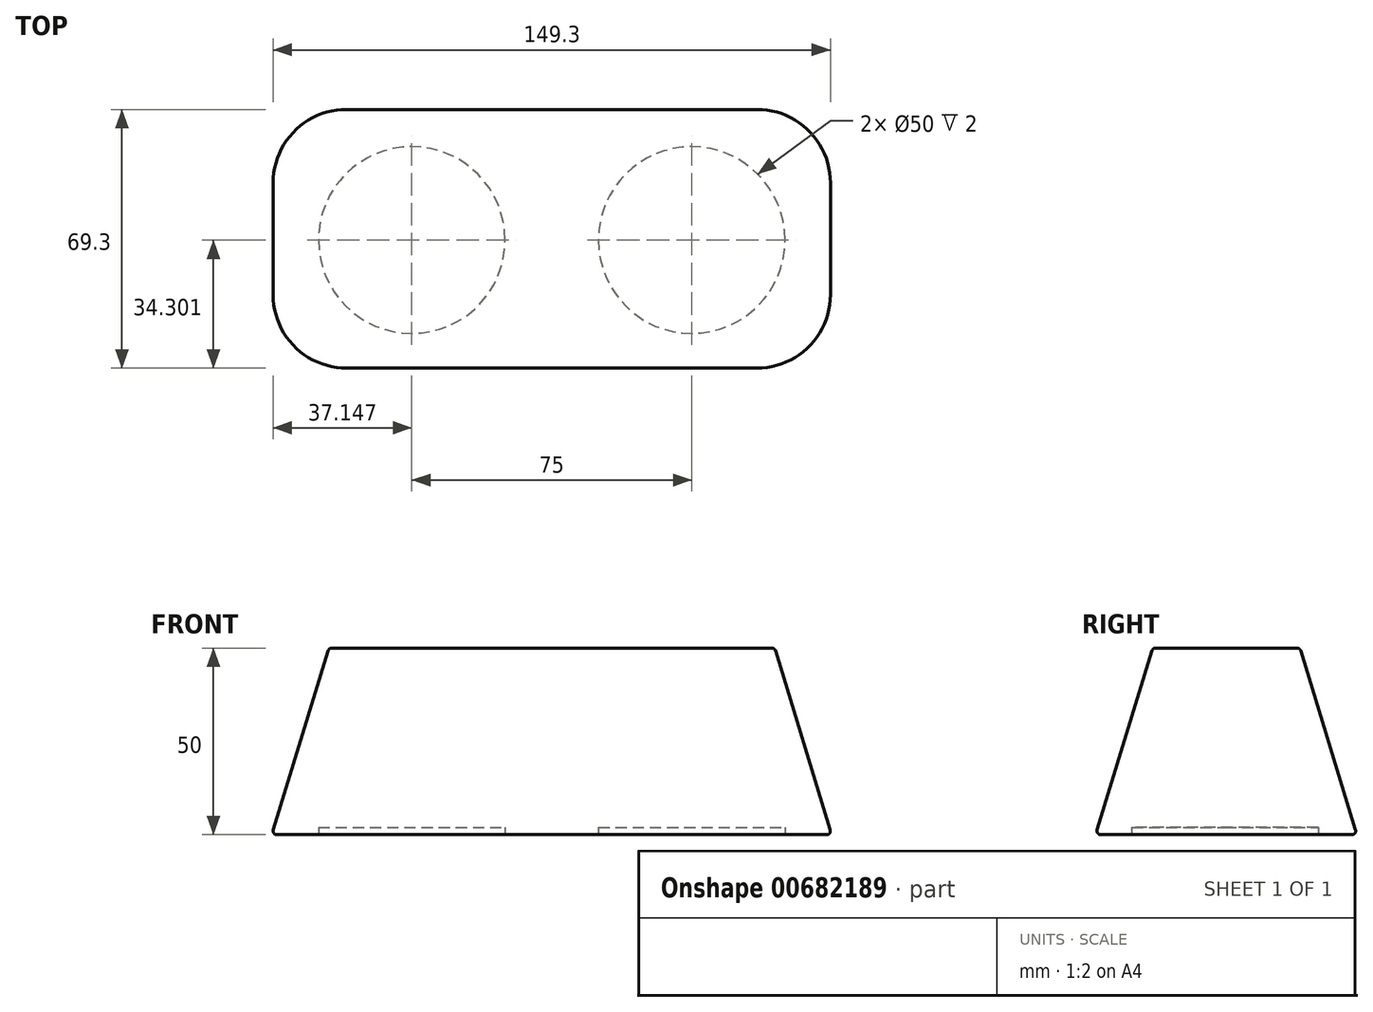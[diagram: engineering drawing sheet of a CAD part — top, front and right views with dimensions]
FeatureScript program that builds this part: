
annotation { "Feature Type Name" : "Feature", "Feature Type Description" : "" }
export const myFeature = defineFeature(function(context is Context, id is Id, definition is map)
    precondition{}
    {
        {
            var Q0;
            Q0=qCreatedBy(makeId("Top.planeOp"),FACE);
            var sketch = newSketch(context, id + "F0", { "sketchPlane" : qUnion([Q0])});
            skLineSegment(sketch, "E0.bottom", {"start": v(-57.37, 55.36) * mm, "end": v(52.63, 55.36) * mm});
            skLineSegment(sketch, "E0.top", {"start": v(-57.37, -14.64) * mm, "end": v(52.63, -14.64) * mm});
            skLineSegment(sketch, "E0.left", {"start": v(-77.37, 35.36) * mm, "end": v(-77.37, 5.36) * mm});
            skLineSegment(sketch, "E0.right", {"start": v(72.63, 35.36) * mm, "end": v(72.63, 5.36) * mm});
            skPoint(sketch, "E1.visualSharp", {"position": v(-77.37, 55.36) * mm});
            skArc(sketch, "E1.filletArc", {"start": v(-57.37, 55.36) * mm, "mid": v(-71.51, 49.5) * mm, "end": v(-77.37, 35.36) * mm});
            skPoint(sketch, "E2.visualSharp", {"position": v(72.63, -14.64) * mm});
            skArc(sketch, "E2.filletArc", {"start": v(52.63, -14.64) * mm, "mid": v(66.77, -8.78) * mm, "end": v(72.63, 5.36) * mm});
            skPoint(sketch, "E3.visualSharp", {"position": v(-77.37, -14.64) * mm});
            skArc(sketch, "E3.filletArc", {"start": v(-77.37, 5.36) * mm, "mid": v(-71.51, -8.78) * mm, "end": v(-57.37, -14.64) * mm});
            skPoint(sketch, "E4.visualSharp", {"position": v(72.63, 55.36) * mm});
            skArc(sketch, "E4.filletArc", {"start": v(72.63, 35.36) * mm, "mid": v(66.77, 49.5) * mm, "end": v(52.63, 55.36) * mm});
            skSolve(sketch);
        }
        {
            var Q0;
            Q0=makeQuery(id+"F0.imprint","IMPRINT",FACE,{"disambiguationData":[TD([[makeQuery(id+"F0.imprint","IMPRINT",EDGE,{"derivedFrom":sQuery(id+"F0.wireOp",EDGE,"E0.bottom")}),-1.0]])]});
            extrude(context, id + "F1", {"entities" : qUnion([Q0]), "depth" : 50 * mm, "offsetDistance" : 25 * mm, "hasDraft" : true, "draftAngle" : 17 * degree, "draftPullDirection" : true});
        }
        {
            var Q0;
            Q0=makeQuery(id+"F1.opExtrude","CAP_FACE",FACE,{"disambiguationData":[OSD([sQuery(id+"F0.wireOp",EDGE,"E0.bottom"),sQuery(id+"F0.wireOp",EDGE,"E0.top"),sQuery(id+"F0.wireOp",EDGE,"E0.left"),sQuery(id+"F0.wireOp",EDGE,"E0.right"),sQuery(id+"F0.wireOp",EDGE,"E1.filletArc"),sQuery(id+"F0.wireOp",EDGE,"E2.filletArc"),sQuery(id+"F0.wireOp",EDGE,"E3.filletArc"),sQuery(id+"F0.wireOp",EDGE,"E4.filletArc")])],"isStart":true});
            var Q1;
            Q1=makeQuery(id+"F1.opExtrude","CAP_FACE",FACE,{"disambiguationData":[OSD([sQuery(id+"F0.wireOp",EDGE,"E0.bottom"),sQuery(id+"F0.wireOp",EDGE,"E0.top"),sQuery(id+"F0.wireOp",EDGE,"E0.left"),sQuery(id+"F0.wireOp",EDGE,"E0.right"),sQuery(id+"F0.wireOp",EDGE,"E1.filletArc"),sQuery(id+"F0.wireOp",EDGE,"E2.filletArc"),sQuery(id+"F0.wireOp",EDGE,"E3.filletArc"),sQuery(id+"F0.wireOp",EDGE,"E4.filletArc")])],"isStart":false});
            fillet(context, id + "F2", {"entities" : qUnion([Q0, Q1]), "radius" : 1 * mm, "tangentPropagation" : true, "allowEdgeOverflow" : false});
        }
        {
            var Q0;
            Q0=makeQuery(id+"F1.opExtrude","CAP_FACE",FACE,{"disambiguationData":[OSD([sQuery(id+"F0.wireOp",EDGE,"E0.bottom"),sQuery(id+"F0.wireOp",EDGE,"E0.top"),sQuery(id+"F0.wireOp",EDGE,"E0.left"),sQuery(id+"F0.wireOp",EDGE,"E0.right"),sQuery(id+"F0.wireOp",EDGE,"E1.filletArc"),sQuery(id+"F0.wireOp",EDGE,"E2.filletArc"),sQuery(id+"F0.wireOp",EDGE,"E3.filletArc"),sQuery(id+"F0.wireOp",EDGE,"E4.filletArc")])],"isStart":true});
            var sketch = newSketch(context, id + "F3", { "sketchPlane" : qUnion([Q0])});
            skCircle(sketch, "E5", {"center": v(35.13, -20.01) * mm, "radius": 25 * mm});
            skCircle(sketch, "E6", {"center": v(-39.87, -20.01) * mm, "radius": 25 * mm});
            skLineSegment(sketch, "E7", {"start": v(35.13, -20.01) * mm, "end": v(-39.87, -20.01) * mm, "construction": true});
            skLineSegment(sketch, "E8", {"start": v(-2.37, -54.01) * mm, "end": v(-2.37, 13.29) * mm, "construction": true});
            skSolve(sketch);
        }
        {
            var Q0;
            Q0 = qSketchRegion(id + "F3", true);
            extrude(context, id + "F4", {"entities" : qUnion([Q0]), "operationType" : NewBodyOperationType.REMOVE, "oppositeDirection" : true, "depth" : 2 * mm, "offsetDistance" : 25 * mm});
        }
    });
